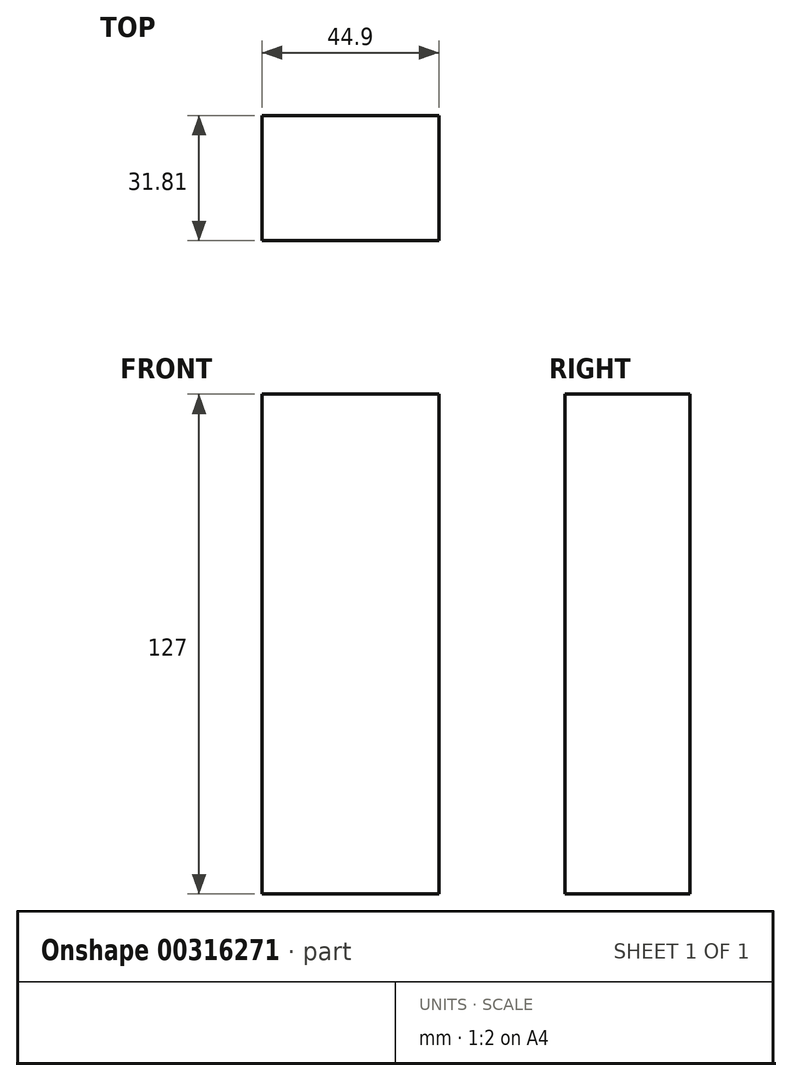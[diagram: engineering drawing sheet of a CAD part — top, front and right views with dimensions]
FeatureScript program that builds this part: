
annotation { "Feature Type Name" : "Feature", "Feature Type Description" : "" }
export const myFeature = defineFeature(function(context is Context, id is Id, definition is map)
    precondition{}
    {
        {
            var Q0;
            Q0=qCreatedBy(makeId("Top.planeOp"),FACE);
            var sketch = newSketch(context, id + "F0", { "sketchPlane" : qUnion([Q0])});
            skLineSegment(sketch, "E0.bottom", {"start": v(0, 0.8) * mm, "end": v(44.9, 0.8) * mm});
            skLineSegment(sketch, "E0.top", {"start": v(0, 32.6) * mm, "end": v(44.9, 32.6) * mm});
            skLineSegment(sketch, "E0.left", {"start": v(0, 0.8) * mm, "end": v(0, 32.6) * mm});
            skLineSegment(sketch, "E0.right", {"start": v(44.9, 0.8) * mm, "end": v(44.9, 32.6) * mm});
            skSolve(sketch);
        }
        {
            var Q0;
            Q0=makeQuery(id+"F0.imprint","IMPRINT",FACE,{"disambiguationData":[TD([[makeQuery(id+"F0.imprint","IMPRINT",EDGE,{"derivedFrom":sQuery(id+"F0.wireOp",EDGE,"E0.bottom")}),1.0]])]});
            extrude(context, id + "F1", {"entities" : qUnion([Q0]), "depth" : 127 * mm});
        }
    });
